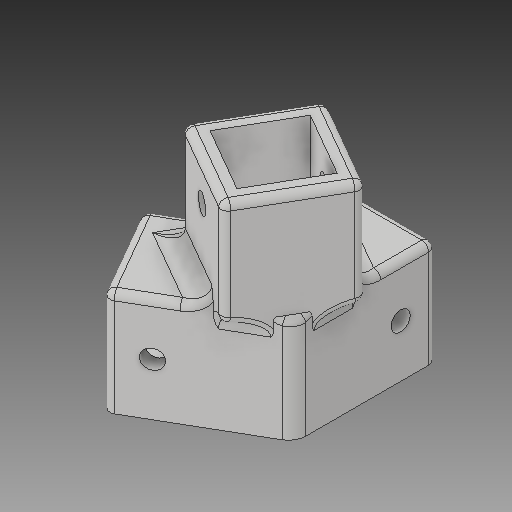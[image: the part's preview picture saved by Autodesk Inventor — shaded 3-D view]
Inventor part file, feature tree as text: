
AUTODESK INVENTOR PART (.ipt)
format: ipt  version: 2019.4 (Build 234330000, 330)  size: 455,680 bytes
history: native  units: mm
features: fillet x12, extrude x8, sketch x8
ambient origin geometry x8: Origin, YZ Plane, XZ Plane, XY Plane, X Axis, Y Axis, Z Axis, Center Point
bodies: Solid1 (feature_tree)
feature tree (28):
  extrude  "Extrusion1"  Depth=40.0mm
  extrude  "Extrusion9"  TaperAngle=60.0deg  [1 undecoded]
  extrude  "Extrusion10"  Depth=30.0mm TaperAngle=0.0deg
  extrude  "Extrusion11"  Depth=21.0mm
  extrude  "Extrusion12"  Depth=21.0mm TaperAngle=0.0deg
  extrude  "Extrusion13"  Depth=21.0mm
  extrude  "Extrusion14"  Depth=21.0mm TaperAngle=0.0deg
  extrude  "Extrusion15"  Depth=5.0mm
  fillet  "Fillet6"  Radius=30.0mm
  fillet  "Fillet7"  Radius=21.0mm
  fillet  "Fillet8"  Radius=21.0mm
  fillet  "Fillet9"  Radius=25.0mm
  fillet  "Fillet10"  Radius=10.0mm
  fillet  "Fillet11"  Radius=5.5mm
  fillet  "Fillet12"  Radius=30.0mm
  fillet  "Fillet13"  Radius=10.0mm
  fillet  "Fillet14"  Radius=5.5mm
  fillet  "Fillet15"  Radius=30.0mm
  fillet  "Fillet16"  Radius=10.0mm
  fillet  "Fillet17"  Radius=5.5mm
  sketch  "Sketch1"  dims[d1=30.0mm d2=40.0mm]
  sketch  "Sketch9"  dims[d3=30.0mm d4=60.0deg]
  sketch  "Sketch10"  dims[d5=40.0mm d6=30.0mm d7=0.0mm]
  sketch  "Sketch11"  dims[d41=15.0mm d42=21.0mm]
  sketch  "Sketch12"  dims[d43=21.0mm d44=25.0mm d45=0.0mm]
  sketch  "Sketch13"  dims[d46=15.0mm d47=21.0mm]
  sketch  "Sketch14"  dims[d48=21.0mm d49=25.0mm d50=0.0mm]
  sketch  "Sketch15"  dims[d51=30.0mm d52=30.0mm d53=30.0mm d54=0.0mm d55=21.0mm d56=21.0mm d57=25.0mm d58=0.0mm d59=10.0mm d60=5.5mm d61=30.0mm d62=0.0mm d63=10.0mm d64=5.5mm d65=30.0mm d66=0.0mm d67=10.0mm d68=5.5mm d69=30.0mm d70=0.0mm d71=5.0mm d72=5.0mm d73=5.0mm d74=5.0mm d75=2.0mm d76=2.0mm d77=2.0mm d78=2.0mm d79=2.0mm d80=2.0mm d81=2.0mm d82=5.0mm]
note: 1 required parameter value undecoded (feature->parameter linkage not recoverable at this tier; creation-order binding heuristic only, values carry confidence <= 0.55)
